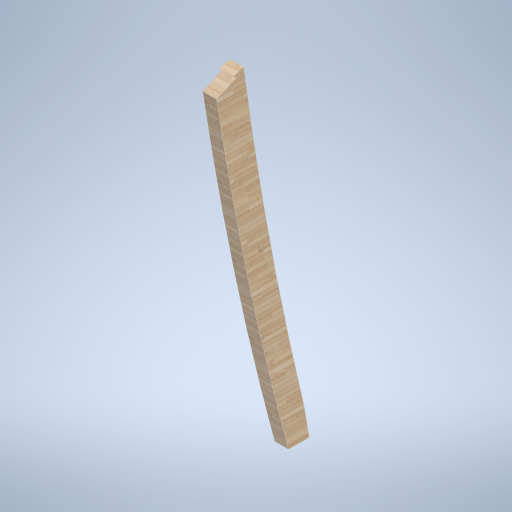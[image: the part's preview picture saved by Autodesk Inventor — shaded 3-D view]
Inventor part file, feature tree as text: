
AUTODESK INVENTOR PART (.ipt)
format: ipt  version: 2024.2 (Build 282272000, 272)  size: 308,224 bytes
history: native  units: mm
features: extrude x1, sketch x1
ambient origin geometry x8: Origin, YZ Plane, XZ Plane, XY Plane, X Axis, Y Axis, Z Axis, Center Point
bodies: Solid1 (feature_tree)
feature tree (2):
  extrude  "Extrusion1"  Depth=40000.0mm
  sketch  "Sketch1"  dims[d0=40000.0mm d1=40000.0mm d2=400.0mm d3=175.0mm d4=0.0mm]
